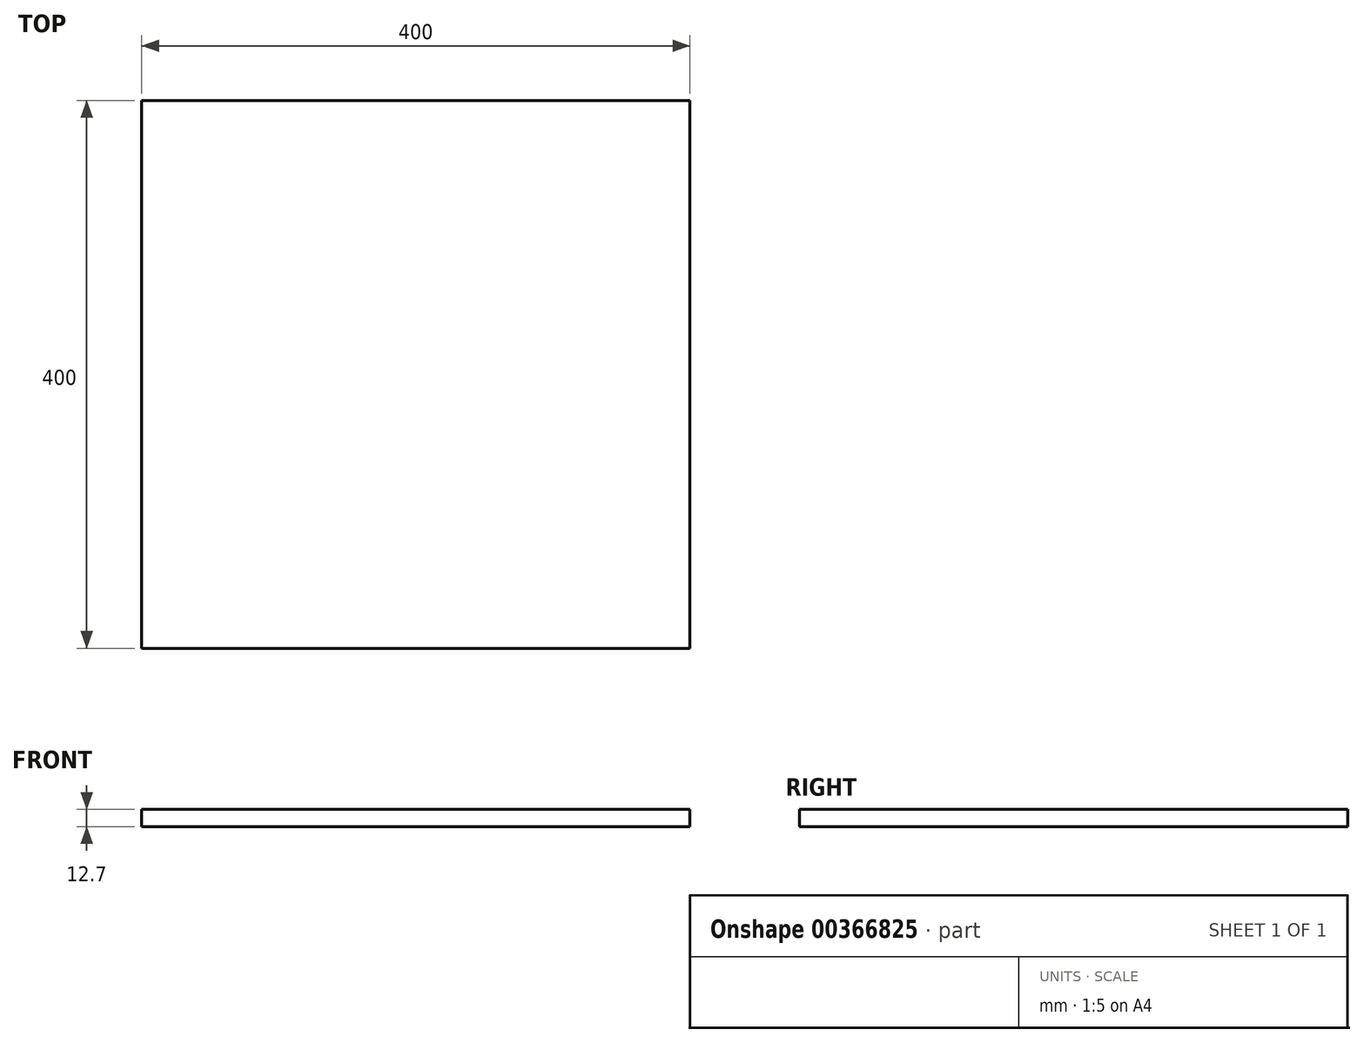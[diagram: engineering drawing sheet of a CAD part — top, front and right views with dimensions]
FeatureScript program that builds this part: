
annotation { "Feature Type Name" : "Feature", "Feature Type Description" : "" }
export const myFeature = defineFeature(function(context is Context, id is Id, definition is map)
    precondition{}
    {
        {
            var Q0;
            Q0=qCreatedBy(makeId("Top.planeOp"),FACE);
            var sketch = newSketch(context, id + "F0", { "sketchPlane" : qUnion([Q0])});
            skLineSegment(sketch, "E0.bottom", {"start": v(-338.11, 218.05) * mm, "end": v(61.89, 218.05) * mm});
            skLineSegment(sketch, "E0.top", {"start": v(-338.11, -181.95) * mm, "end": v(61.89, -181.95) * mm});
            skLineSegment(sketch, "E0.left", {"start": v(-338.11, 218.05) * mm, "end": v(-338.11, -181.95) * mm});
            skLineSegment(sketch, "E0.right", {"start": v(61.89, 218.05) * mm, "end": v(61.89, -181.95) * mm});
            skSolve(sketch);
        }
        {
            var Q0;
            Q0=makeQuery(id+"F0.imprint","IMPRINT",FACE,{"disambiguationData":[TD([[makeQuery(id+"F0.imprint","IMPRINT",EDGE,{"derivedFrom":sQuery(id+"F0.wireOp",EDGE,"E0.bottom")}),-1.0]])]});
            extrude(context, id + "F1", {"entities" : qUnion([Q0]), "depth" : 12.7 * mm});
        }
    });
